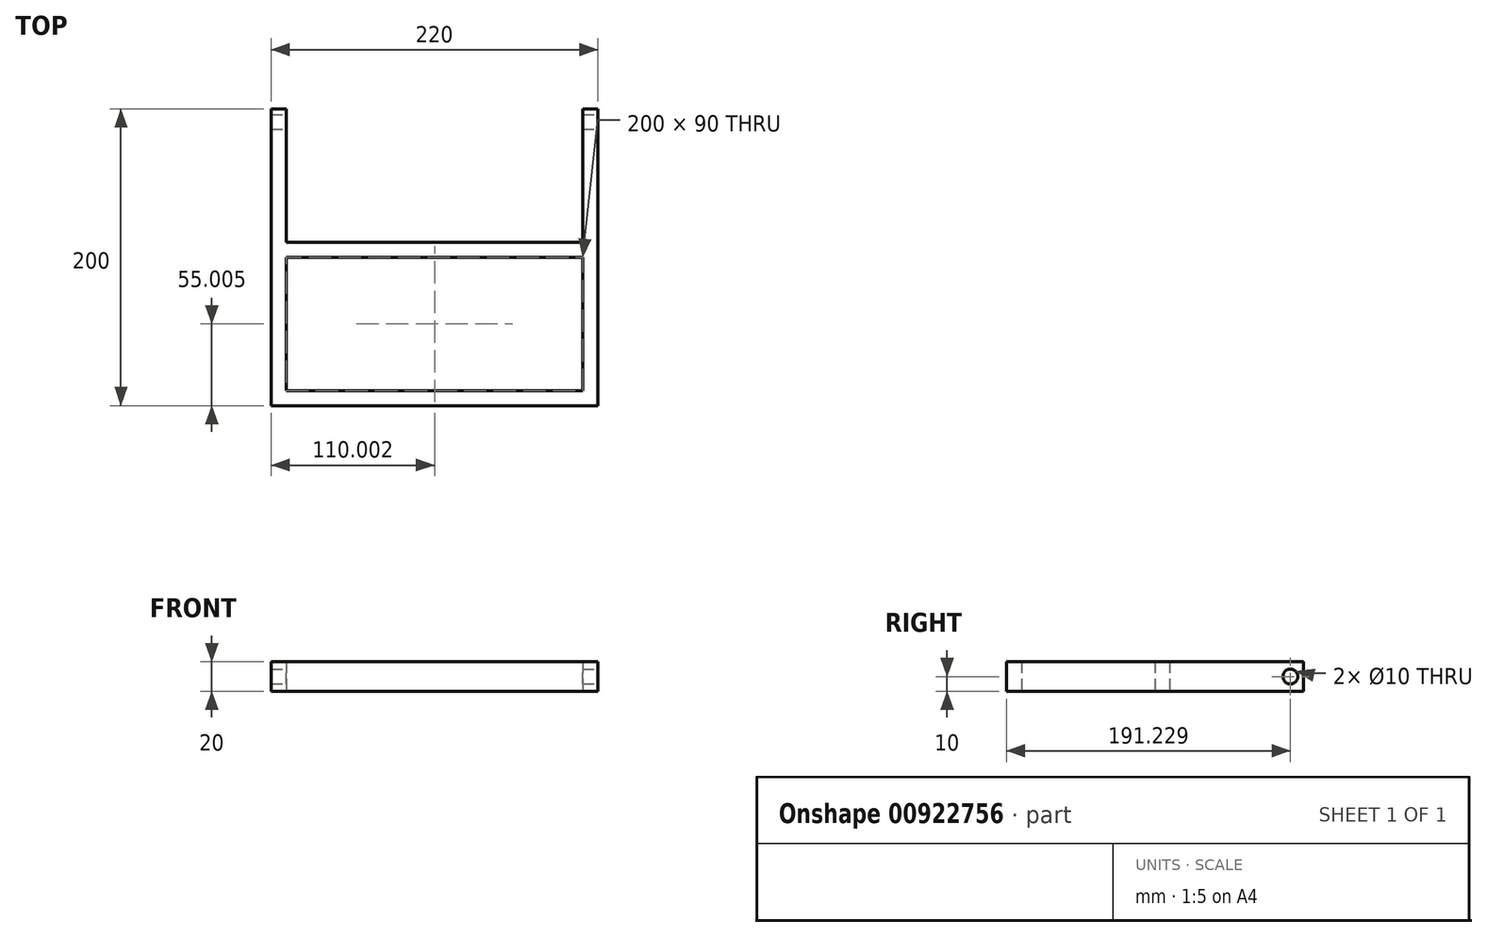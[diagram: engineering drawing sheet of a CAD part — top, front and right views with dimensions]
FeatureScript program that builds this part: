
annotation { "Feature Type Name" : "Feature", "Feature Type Description" : "" }
export const myFeature = defineFeature(function(context is Context, id is Id, definition is map)
    precondition{}
    {
        {
            var Q0;
            Q0=qCreatedBy(makeId("Top.planeOp"),FACE);
            var sketch = newSketch(context, id + "F0", { "sketchPlane" : qUnion([Q0])});
            skLineSegment(sketch, "E0.bottom", {"start": v(-44.68, 127.92) * mm, "end": v(-54.68, 127.92) * mm});
            skLineSegment(sketch, "E0.top", {"start": v(-44.68, -72.08) * mm, "end": v(-54.68, -72.08) * mm});
            skLineSegment(sketch, "E0.left", {"start": v(-44.68, 127.92) * mm, "end": v(-44.68, -72.08) * mm});
            skLineSegment(sketch, "E0.right", {"start": v(-54.68, 127.92) * mm, "end": v(-54.68, -72.08) * mm});
            skLineSegment(sketch, "E1.bottom", {"start": v(155.32, 127.92) * mm, "end": v(165.32, 127.92) * mm});
            skLineSegment(sketch, "E1.top", {"start": v(155.32, -72.08) * mm, "end": v(165.32, -72.08) * mm});
            skLineSegment(sketch, "E1.left", {"start": v(155.32, 127.92) * mm, "end": v(155.32, -72.08) * mm});
            skLineSegment(sketch, "E1.right", {"start": v(165.32, 127.92) * mm, "end": v(165.32, -72.08) * mm});
            skLineSegment(sketch, "E2.bottom", {"start": v(-44.68, -72.08) * mm, "end": v(155.32, -72.08) * mm});
            skLineSegment(sketch, "E2.top", {"start": v(-44.68, -62.08) * mm, "end": v(155.32, -62.08) * mm});
            skLineSegment(sketch, "E2.left", {"start": v(-44.68, -72.08) * mm, "end": v(-44.68, -62.08) * mm});
            skLineSegment(sketch, "E2.right", {"start": v(155.32, -72.08) * mm, "end": v(155.32, -62.08) * mm});
            skLineSegment(sketch, "E3.bottom", {"start": v(-44.68, 37.92) * mm, "end": v(155.32, 37.92) * mm});
            skLineSegment(sketch, "E3.top", {"start": v(-44.68, 27.92) * mm, "end": v(155.32, 27.92) * mm});
            skLineSegment(sketch, "E3.left", {"start": v(-44.68, 37.92) * mm, "end": v(-44.68, 27.92) * mm});
            skLineSegment(sketch, "E3.right", {"start": v(155.32, 37.92) * mm, "end": v(155.32, 27.92) * mm});
            skSolve(sketch);
        }
        {
            var Q0;
            Q0 = qSketchRegion(id + "F0", true);
            extrude(context, id + "F1", {"entities" : qUnion([Q0]), "depth" : 20 * mm, "offsetDistance" : 25 * mm});
        }
        {
            var Q0;
            Q0=makeQuery(id+"F1.opExtrude","SWEPT_FACE",FACE,{"disambiguationData":[OSD([sQuery(id+"F0.wireOp",EDGE,"E1.right")])]});
            var sketch = newSketch(context, id + "F2", { "sketchPlane" : qUnion([Q0])});
            skCircle(sketch, "E4", {"center": v(119.15, 10) * mm, "radius": 5 * mm});
            skSolve(sketch);
        }
        {
            var Q0;
            Q0 = qSketchRegion(id + "F2", true);
            extrude(context, id + "F3", {"entities" : qUnion([Q0]), "operationType" : NewBodyOperationType.REMOVE, "oppositeDirection" : true, "depth" : 563 * mm, "offsetDistance" : 25 * mm});
        }
    });
